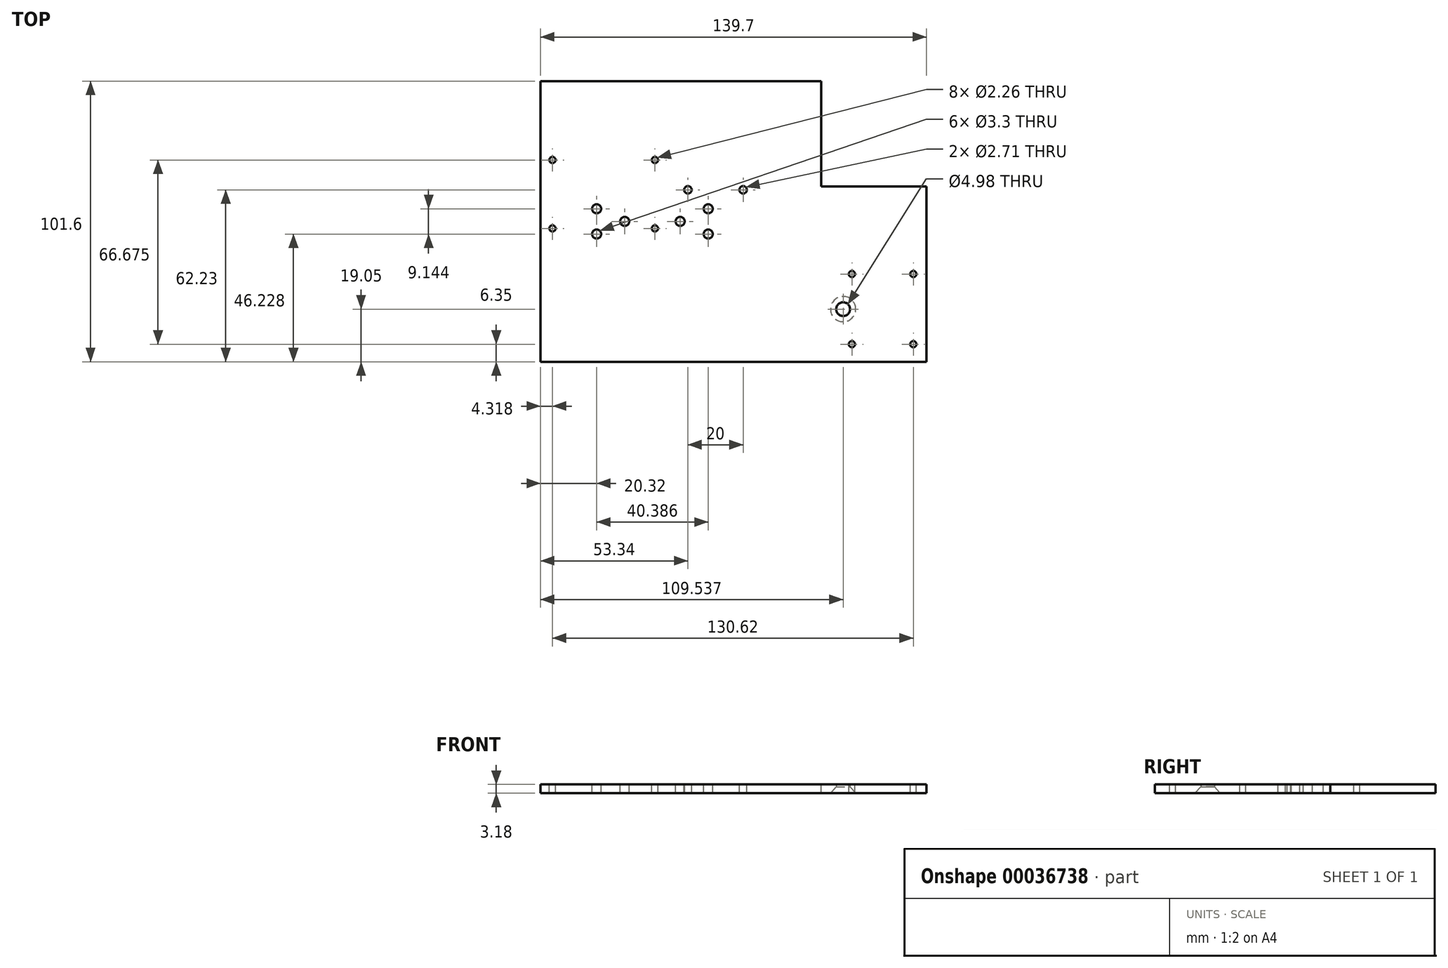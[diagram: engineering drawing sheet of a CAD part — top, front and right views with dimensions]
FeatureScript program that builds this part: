
annotation { "Feature Type Name" : "Feature", "Feature Type Description" : "" }
export const myFeature = defineFeature(function(context is Context, id is Id, definition is map)
    precondition{}
    {
        {
            var Q0;
            Q0=qCreatedBy(makeId("Front.planeOp"),FACE);
            var sketch = newSketch(context, id + "F0", { "sketchPlane" : qUnion([Q0])});
            skLineSegment(sketch, "E0", {"start": v(0, 0) * mm, "end": v(0, 3.18) * mm});
            skLineSegment(sketch, "E1", {"start": v(0, 3.18) * mm, "end": v(-139.7, 3.17) * mm});
            skLineSegment(sketch, "E2", {"start": v(-139.7, 3.18) * mm, "end": v(-139.7, 0) * mm});
            skLineSegment(sketch, "E3", {"start": v(-139.7, 0) * mm, "end": v(0, 0) * mm});
            skSolve(sketch);
        }
        {
            var Q0;
            Q0=makeQuery(id+"F0.imprint","IMPRINT",FACE,{"disambiguationData":[TD([[makeQuery(id+"F0.imprint","IMPRINT",EDGE,{"derivedFrom":sQuery(id+"F0.wireOp",EDGE,"E0")}),1.0]])]});
            extrude(context, id + "F1", {"entities" : qUnion([Q0]), "endBound" : BoundingType.SYMMETRIC, "depth" : 101.6 * mm, "offsetDistance" : 25.4 * mm});
        }
        {
            var Q0;
            Q0=makeQuery(id+"F1.opExtrude","SWEPT_FACE",FACE,{"disambiguationData":[OSD([sQuery(id+"F0.wireOp",EDGE,"E1")])]});
            var sketch = newSketch(context, id + "F2", { "sketchPlane" : qUnion([Q0])});
            skPoint(sketch, "E4", {"position": v(-119.38, 4.57) * mm});
            skPoint(sketch, "E5", {"position": v(-119.38, -4.57) * mm});
            skPoint(sketch, "E6", {"position": v(-109.22, 0) * mm});
            skPoint(sketch, "E7", {"position": v(-89.15, 0) * mm});
            skPoint(sketch, "E8", {"position": v(-79, 4.57) * mm});
            skPoint(sketch, "E9", {"position": v(-79, -4.57) * mm});
            skLineSegment(sketch, "E10", {"start": v(-139.7, 0) * mm, "end": v(-58.67, 0) * mm, "construction": true});
            skLineSegment(sketch, "E11", {"start": v(-99.19, 0) * mm, "end": v(-99.19, 9.55) * mm, "construction": true});
            skSolve(sketch);
        }
        {
            var Q0;
            Q0=sQuery(id+"F2.wireOp",VERTEX,"E8");
            var Q1;
            Q1=sQuery(id+"F2.wireOp",VERTEX,"E9");
            var Q2;
            Q2=sQuery(id+"F2.wireOp",VERTEX,"E7");
            var Q3;
            Q3=sQuery(id+"F2.wireOp",VERTEX,"E6");
            var Q4;
            Q4=sQuery(id+"F2.wireOp",VERTEX,"E4");
            var Q5;
            Q5=sQuery(id+"F2.wireOp",VERTEX,"E5");
            var Q6;
            Q6=makeQuery(id+"F1.opExtrude","SWEPT_BODY",BODY,{"disambiguationData":[OSD([sQuery(id+"F0.wireOp",EDGE,"E0"),sQuery(id+"F0.wireOp",EDGE,"f2e0e0e0-cd28-4836-966f-49551ec3c4cd"),sQuery(id+"F0.wireOp",EDGE,"6f173ce0-8d91-4cf6-bb4e-4d458c8b243f"),sQuery(id+"F0.wireOp",EDGE,"E1"),sQuery(id+"F0.wireOp",EDGE,"E2"),sQuery(id+"F0.wireOp",EDGE,"E3")])]});
            hole(context, id + "F3", {"style" : HoleStyle.SIMPLE, "endStyle" : HoleEndStyle.THROUGH, "holeDiameter" : 3.3 * mm, "majorDiameter" : 6.35 * mm, "tappedDepth" : 6.35 * mm, "tapClearance" : 3, "locations" : qUnion([Q0, Q1, Q2, Q3, Q4, Q5]), "scope" : qUnion([Q6])});
        }
        {
            var Q0;
            Q0=makeQuery(id+"F1.opExtrude","SWEPT_FACE",FACE,{"disambiguationData":[OSD([sQuery(id+"F0.wireOp",EDGE,"E1")])]});
            var sketch = newSketch(context, id + "F4", { "sketchPlane" : qUnion([Q0])});
            skLineSegment(sketch, "E12.bottom", {"start": v(0, 50.8) * mm, "end": v(-38.1, 50.8) * mm});
            skLineSegment(sketch, "E12.top", {"start": v(0, 12.7) * mm, "end": v(-38.1, 12.7) * mm});
            skLineSegment(sketch, "E12.left", {"start": v(0, 50.8) * mm, "end": v(0, 12.7) * mm});
            skLineSegment(sketch, "E12.right", {"start": v(-38.1, 50.8) * mm, "end": v(-38.1, 12.7) * mm});
            skSolve(sketch);
        }
        {
            var Q0;
            Q0=makeQuery(id+"F4.imprint","IMPRINT",FACE,{"disambiguationData":[TD([[makeQuery(id+"F4.imprint","IMPRINT",EDGE,{"derivedFrom":sQuery(id+"F4.wireOp",EDGE,"E12.bottom")}),1.0]])]});
            extrude(context, id + "F5", {"entities" : qUnion([Q0]), "operationType" : NewBodyOperationType.REMOVE, "endBound" : BoundingType.THROUGH_ALL, "oppositeDirection" : true, "depth" : 25.4 * mm, "offsetDistance" : 25.4 * mm});
        }
        {
            var Q0;
            Q0=makeQuery(id+"F1.opExtrude","SWEPT_FACE",FACE,{"disambiguationData":[OSD([sQuery(id+"F0.wireOp",EDGE,"E1")])]});
            var sketch = newSketch(context, id + "F6", { "sketchPlane" : qUnion([Q0])});
            skPoint(sketch, "E13", {"position": v(-4.76, -44.45) * mm});
            skPoint(sketch, "E14", {"position": v(-26.99, -44.45) * mm});
            skPoint(sketch, "E15", {"position": v(-26.99, -19.05) * mm});
            skPoint(sketch, "E16", {"position": v(-4.76, -19.05) * mm});
            skSolve(sketch);
        }
        {
            var Q0;
            Q0=sQuery(id+"F6.wireOp",VERTEX,"E14");
            var Q1;
            Q1=sQuery(id+"F6.wireOp",VERTEX,"E15");
            var Q2;
            Q2=sQuery(id+"F6.wireOp",VERTEX,"E16");
            var Q3;
            Q3=sQuery(id+"F6.wireOp",VERTEX,"E13");
            var Q4;
            Q4=makeQuery(id+"F1.opExtrude","SWEPT_BODY",BODY,{"disambiguationData":[OSD([sQuery(id+"F0.wireOp",EDGE,"E0"),sQuery(id+"F0.wireOp",EDGE,"E1"),sQuery(id+"F0.wireOp",EDGE,"E2"),sQuery(id+"F0.wireOp",EDGE,"E3")])]});
            hole(context, id + "F7", {"style" : HoleStyle.SIMPLE, "endStyle" : HoleEndStyle.THROUGH, "standardTappedOrClearance" : lookupTablePath({ "standard" : "ANSI", "engagement" : "75%", "pitch" : "40 tpi", "size" : "#4", "type" : "Tapped" }), "standardBlindInLast" : lookupTablePath({ "standard" : "ANSI", "engagement" : "75%", "pitch" : "40 tpi", "size" : "#4", "type" : "Tapped" }), "holeDiameter" : 2.26 * mm, "majorDiameter" : 2.84 * mm, "showTappedDepth" : true, "tappedDepth" : 6.35 * mm, "tapClearance" : 3, "locations" : qUnion([Q0, Q1, Q2, Q3]), "scope" : qUnion([Q4])});
        }
        {
            var Q0;
            Q0=makeQuery(id+"F1.opExtrude","SWEPT_FACE",FACE,{"disambiguationData":[OSD([sQuery(id+"F0.wireOp",EDGE,"E1")])]});
            var sketch = newSketch(context, id + "F8", { "sketchPlane" : qUnion([Q0])});
            skPoint(sketch, "E17", {"position": v(-86.36, 11.43) * mm});
            skPoint(sketch, "E18", {"position": v(-66.36, 11.43) * mm});
            skSolve(sketch);
        }
        {
            var Q0;
            Q0=sQuery(id+"F8.wireOp",VERTEX,"E17");
            var Q1;
            Q1=sQuery(id+"F8.wireOp",VERTEX,"E18");
            var Q2;
            Q2=makeQuery(id+"F1.opExtrude","SWEPT_BODY",BODY,{"disambiguationData":[OSD([sQuery(id+"F0.wireOp",EDGE,"E0"),sQuery(id+"F0.wireOp",EDGE,"E1"),sQuery(id+"F0.wireOp",EDGE,"E2"),sQuery(id+"F0.wireOp",EDGE,"E3")])]});
            hole(context, id + "F9", {"style" : HoleStyle.SIMPLE, "endStyle" : HoleEndStyle.THROUGH, "standardTappedOrClearance" : lookupTablePath({ "standard" : "ANSI", "engagement" : "75%", "pitch" : "32 tpi", "size" : "#6", "type" : "Tapped" }), "standardBlindInLast" : lookupTablePath({ "standard" : "ANSI", "engagement" : "75%", "pitch" : "32 tpi", "size" : "#6", "type" : "Tapped" }), "holeDiameter" : 2.7 * mm, "majorDiameter" : 3.5 * mm, "showTappedDepth" : true, "isTappedThrough" : true, "tappedDepth" : 10.3 * mm, "tapClearance" : 3, "locations" : qUnion([Q0, Q1]), "scope" : qUnion([Q2])});
        }
        {
            var Q0;
            Q0=makeQuery(id+"F1.opExtrude","SWEPT_FACE",FACE,{"disambiguationData":[OSD([sQuery(id+"F0.wireOp",EDGE,"E1")])]});
            var sketch = newSketch(context, id + "F10", { "sketchPlane" : qUnion([Q0])});
            skPoint(sketch, "E19", {"position": v(-135.38, -2.54) * mm});
            skPoint(sketch, "E20", {"position": v(-135.38, 22.23) * mm});
            skPoint(sketch, "E21", {"position": v(-98.3, -2.54) * mm});
            skPoint(sketch, "E22", {"position": v(-98.3, 22.23) * mm});
            skSolve(sketch);
        }
        {
            var Q0;
            Q0=sQuery(id+"F10.wireOp",VERTEX,"E19");
            var Q1;
            Q1=sQuery(id+"F10.wireOp",VERTEX,"E21");
            var Q2;
            Q2=sQuery(id+"F10.wireOp",VERTEX,"E22");
            var Q3;
            Q3=sQuery(id+"F10.wireOp",VERTEX,"E20");
            var Q4;
            Q4=makeQuery(id+"F1.opExtrude","SWEPT_BODY",BODY,{"disambiguationData":[OSD([sQuery(id+"F0.wireOp",EDGE,"E0"),sQuery(id+"F0.wireOp",EDGE,"E1"),sQuery(id+"F0.wireOp",EDGE,"E2"),sQuery(id+"F0.wireOp",EDGE,"E3")])]});
            hole(context, id + "F11", {"style" : HoleStyle.SIMPLE, "endStyle" : HoleEndStyle.THROUGH, "standardTappedOrClearance" : lookupTablePath({ "standard" : "ANSI", "engagement" : "75%", "pitch" : "40 tpi", "size" : "#4", "type" : "Tapped" }), "standardBlindInLast" : lookupTablePath({ "standard" : "ANSI", "engagement" : "75%", "pitch" : "40 tpi", "size" : "#4", "type" : "Tapped" }), "holeDiameter" : 2.26 * mm, "majorDiameter" : 2.84 * mm, "showTappedDepth" : true, "isTappedThrough" : true, "tappedDepth" : 10.3 * mm, "tapClearance" : 3, "locations" : qUnion([Q0, Q1, Q2, Q3]), "scope" : qUnion([Q4])});
        }
        {
            var Q0;
            Q0=makeQuery(id+"F1.opExtrude","SWEPT_FACE",FACE,{"disambiguationData":[OSD([sQuery(id+"F0.wireOp",EDGE,"E3")])]});
            var sketch = newSketch(context, id + "F12", { "sketchPlane" : qUnion([Q0])});
            skPoint(sketch, "E23", {"position": v(-30.16, 31.75) * mm});
            skCircle(sketch, "E24.0", {"center": v(-26.99, 44.45) * mm, "radius": 1.13 * mm});
            skSolve(sketch);
        }
        {
            var Q0;
            Q0=sQuery(id+"F12.wireOp",VERTEX,"E23");
            var Q1;
            Q1=makeQuery(id+"F1.opExtrude","SWEPT_BODY",BODY,{"disambiguationData":[OSD([sQuery(id+"F0.wireOp",EDGE,"E0"),sQuery(id+"F0.wireOp",EDGE,"E1"),sQuery(id+"F0.wireOp",EDGE,"E2"),sQuery(id+"F0.wireOp",EDGE,"E3")])]});
            hole(context, id + "F13", {"style" : HoleStyle.C_SINK, "endStyle" : HoleEndStyle.THROUGH, "standardTappedOrClearance" : lookupTablePath({ "fit" : "Normal (ASME)", "standard" : "ANSI", "size" : "#8", "type" : "Clearance" }), "standardBlindInLast" : lookupTablePath({ "fit" : "Normal", "standard" : "ANSI", "size" : "#8", "type" : "Clearance" }), "holeDiameter" : 4.98 * mm, "cSinkDiameter" : 9.12 * mm, "cSinkAngle" : 82 * degree, "majorDiameter" : 6.35 * mm, "isTappedThrough" : true, "tappedDepth" : 6.35 * mm, "tapClearance" : 3, "locations" : qUnion([Q0]), "scope" : qUnion([Q1])});
        }
    });
